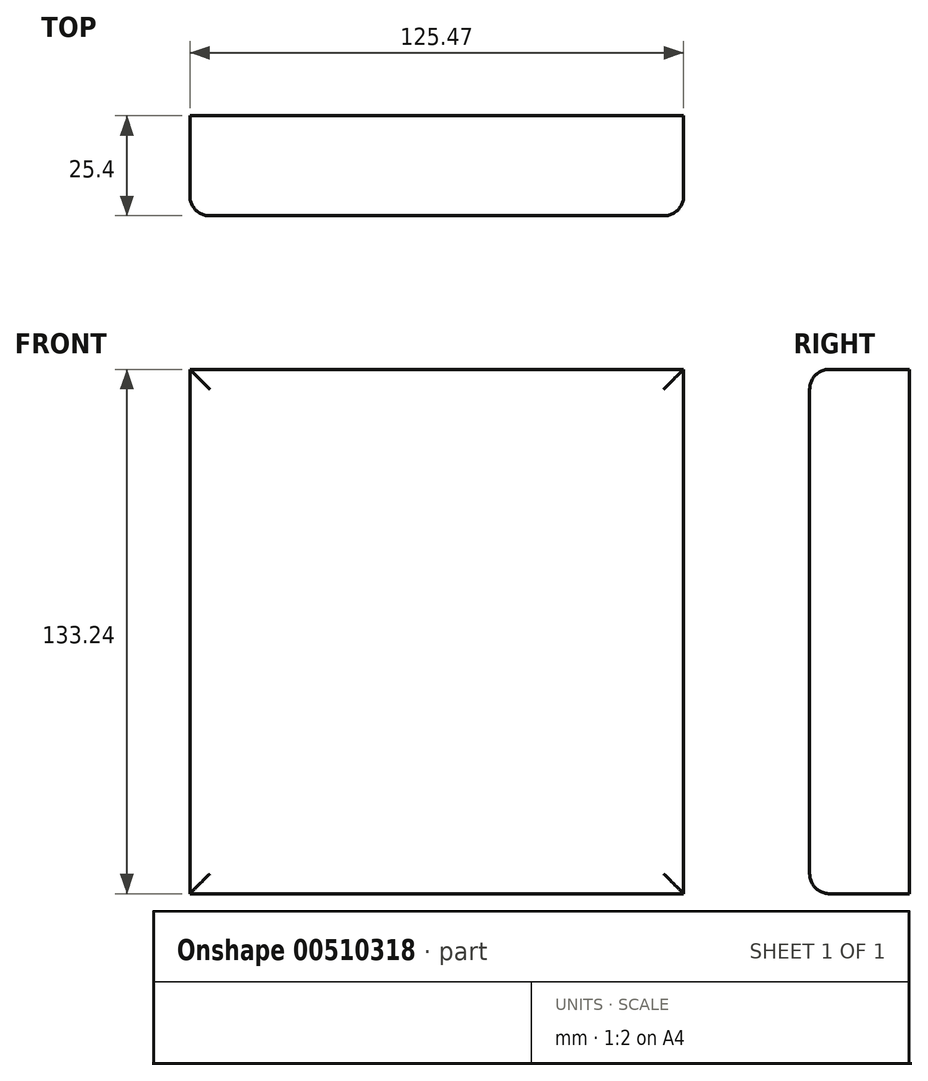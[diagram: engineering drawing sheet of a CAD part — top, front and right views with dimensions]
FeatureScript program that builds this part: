
annotation { "Feature Type Name" : "Feature", "Feature Type Description" : "" }
export const myFeature = defineFeature(function(context is Context, id is Id, definition is map)
    precondition{}
    {
        {
            var Q0;
            Q0=qCreatedBy(makeId("Front.planeOp"),FACE);
            var sketch = newSketch(context, id + "F0", { "sketchPlane" : qUnion([Q0])});
            skLineSegment(sketch, "E0.bottom", {"start": v(0, -21.46) * mm, "end": v(-125.47, -21.46) * mm});
            skLineSegment(sketch, "E0.top", {"start": v(0, 111.78) * mm, "end": v(-125.47, 111.78) * mm});
            skLineSegment(sketch, "E0.left", {"start": v(0, -21.46) * mm, "end": v(0, 111.78) * mm});
            skLineSegment(sketch, "E0.right", {"start": v(-125.47, -21.46) * mm, "end": v(-125.47, 111.78) * mm});
            skPoint(sketch, "E0.middle", {"position": v(-62.73, 45.16) * mm});
            skSolve(sketch);
        }
        {
            var Q0;
            Q0=makeQuery(id+"F0.imprint","IMPRINT",FACE,{"disambiguationData":[TD([[makeQuery(id+"F0.imprint","IMPRINT",EDGE,{"derivedFrom":sQuery(id+"F0.wireOp",EDGE,"E0.bottom")}),-1.0]])]});
            extrude(context, id + "F1", {"entities" : qUnion([Q0]), "depth" : 25.4 * mm});
        }
        {
            var Q0;
            Q0=makeQuery(id+"F1.opExtrude","CAP_EDGE",EDGE,{"disambiguationData":[OSD([sQuery(id+"F0.wireOp",EDGE,"E0.top")])],"isStart":false});
            var Q1;
            Q1=makeQuery(id+"F1.opExtrude","CAP_EDGE",EDGE,{"disambiguationData":[OSD([sQuery(id+"F0.wireOp",EDGE,"E0.left")])],"isStart":false});
            var Q2;
            Q2=makeQuery(id+"F1.opExtrude","CAP_EDGE",EDGE,{"disambiguationData":[OSD([sQuery(id+"F0.wireOp",EDGE,"E0.right")])],"isStart":false});
            var Q3;
            Q3=makeQuery(id+"F1.opExtrude","CAP_EDGE",EDGE,{"disambiguationData":[OSD([sQuery(id+"F0.wireOp",EDGE,"E0.bottom")])],"isStart":false});
            fillet(context, id + "F2", {"entities" : qUnion([Q0, Q1, Q2, Q3]), "radius" : 5.08 * mm, "tangentPropagation" : true, "allowEdgeOverflow" : false});
        }
    });
